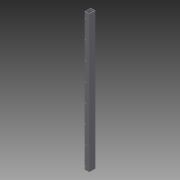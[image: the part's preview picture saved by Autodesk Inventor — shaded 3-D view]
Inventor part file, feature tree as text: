
AUTODESK INVENTOR PART (.ipt)
format: ipt  version: 2013 (Build 170138000, 138)  size: 136,704 bytes
history: native  units: in
note: dims shown in document units (in); Inventor stores cm internally (conversion verified against a paired STEP export)
features: other x4, extrude x1, sketch x1
ambient origin geometry x8: Origin, YZ Plane, XZ Plane, XY Plane, X Axis, Y Axis, Z Axis, Center Point
bodies: Solid1 (feature_tree)
feature tree (6):
  other  "Table"
  other  "squareTube1.5x2.ipt"
  extrude  "Extrusion2"  TaperAngle=0.0deg  [1 undecoded]
  other  "Solid1::squareTube1.5x2.ipt"
  other  "TaggingFeature1"
  sketch  "Sketch2"  dims[d0=1.5in d1=2.0in d2=0.125in d4=0.0in d16=0.125in d18=0.5in d19=1.0in d20=3.1496in d22=6.0in d23=0.3937in d25=1.0in d27=1.875in d28=0.0in]
note: 1 required parameter value undecoded (feature->parameter linkage not recoverable at this tier; creation-order binding heuristic only, values carry confidence <= 0.55)
